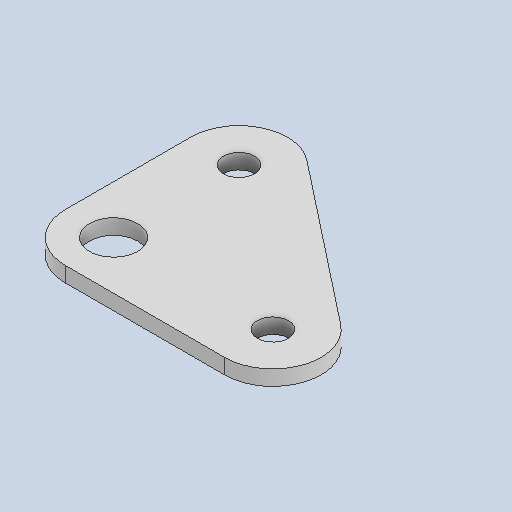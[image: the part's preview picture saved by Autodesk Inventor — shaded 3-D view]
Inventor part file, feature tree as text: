
AUTODESK INVENTOR PART (.ipt)
format: ipt  version: 2024.2 (Build 282272000, 272)  size: 89,088 bytes
history: native  units: in
note: dims shown in document units (in); Inventor stores cm internally (conversion verified against a paired STEP export)
features: fillet x1
ambient origin geometry x8: Origin, YZ Plane, XZ Plane, XY Plane, X Axis, Y Axis, Z Axis, Center Point
bodies: Solid1 (feature_tree)
feature tree (1):
  fillet  "Fillet1"  [1 undecoded]
note: 1 required parameter value undecoded (feature->parameter linkage not recoverable at this tier; creation-order binding heuristic only, values carry confidence <= 0.55)
